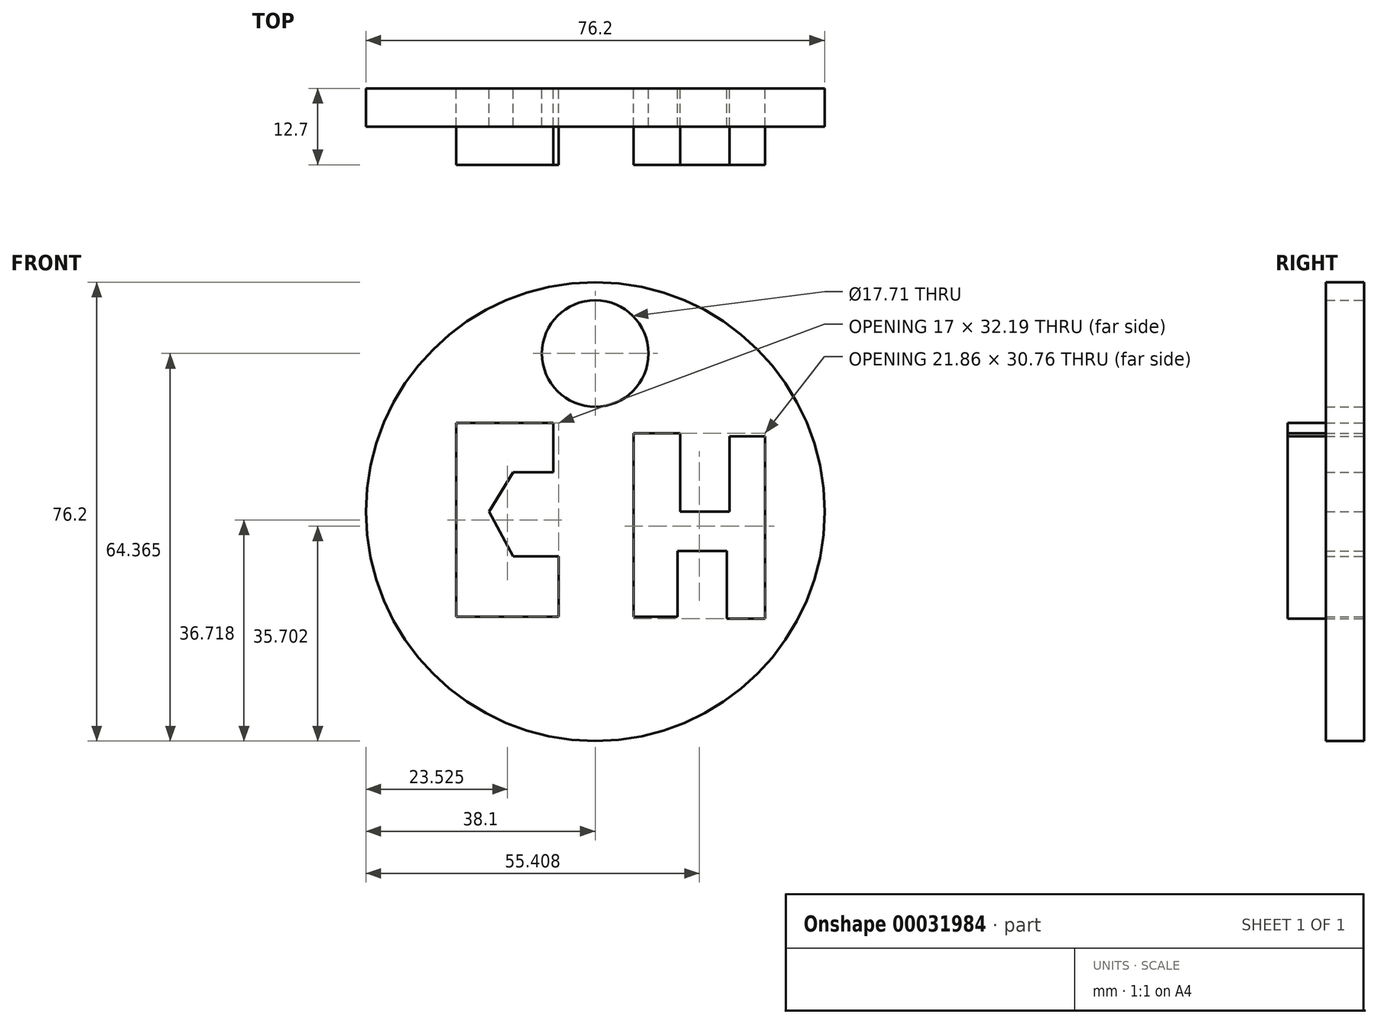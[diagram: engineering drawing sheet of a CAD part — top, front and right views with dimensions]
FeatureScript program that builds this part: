
annotation { "Feature Type Name" : "Feature", "Feature Type Description" : "" }
export const myFeature = defineFeature(function(context is Context, id is Id, definition is map)
    precondition{}
    {
        {
            var Q0;
            Q0=qCreatedBy(makeId("Front.planeOp"),FACE);
            var sketch = newSketch(context, id + "F0", { "sketchPlane" : qUnion([Q0])});
            skCircle(sketch, "E0", {"center": v(0, 0) * mm, "radius": 38.1 * mm});
            skLineSegment(sketch, "E1", {"start": v(6.38, 12.98) * mm, "end": v(14.12, 12.98) * mm});
            skLineSegment(sketch, "E2", {"start": v(14.12, 12.98) * mm, "end": v(14.12, 0) * mm});
            skLineSegment(sketch, "E3", {"start": v(14.12, 0) * mm, "end": v(22.32, 0) * mm});
            skLineSegment(sketch, "E4", {"start": v(22.32, 0) * mm, "end": v(22.32, 12.53) * mm});
            skLineSegment(sketch, "E5", {"start": v(22.32, 12.53) * mm, "end": v(28.24, 12.53) * mm});
            skLineSegment(sketch, "E6", {"start": v(28.24, 12.53) * mm, "end": v(28.24, -17.78) * mm});
            skLineSegment(sketch, "E7", {"start": v(28.24, -17.78) * mm, "end": v(21.86, -17.78) * mm});
            skLineSegment(sketch, "E8", {"start": v(21.86, -17.78) * mm, "end": v(21.86, -6.54) * mm});
            skLineSegment(sketch, "E9", {"start": v(21.86, -6.54) * mm, "end": v(13.66, -6.54) * mm});
            skLineSegment(sketch, "E10", {"start": v(13.66, -6.54) * mm, "end": v(13.66, -17.47) * mm});
            skLineSegment(sketch, "E11", {"start": v(13.66, -17.47) * mm, "end": v(6.38, -17.47) * mm});
            skLineSegment(sketch, "E12", {"start": v(6.38, -17.47) * mm, "end": v(6.38, 12.98) * mm});
            skLineSegment(sketch, "E13", {"start": v(-6.98, 14.71) * mm, "end": v(-23.08, 14.71) * mm});
            skLineSegment(sketch, "E14", {"start": v(-23.08, 14.71) * mm, "end": v(-23.08, -17.48) * mm});
            skLineSegment(sketch, "E15", {"start": v(-23.08, -17.48) * mm, "end": v(-6.07, -17.48) * mm});
            skLineSegment(sketch, "E16", {"start": v(-6.07, -17.48) * mm, "end": v(-6.07, -7.44) * mm});
            skLineSegment(sketch, "E17", {"start": v(-6.07, -7.44) * mm, "end": v(-13.66, -7.44) * mm});
            skLineSegment(sketch, "E18", {"start": v(-13.66, -7.44) * mm, "end": v(-17.61, 0) * mm});
            skLineSegment(sketch, "E19", {"start": v(-17.61, 0) * mm, "end": v(-13.66, 6.53) * mm});
            skLineSegment(sketch, "E20", {"start": v(-13.66, 6.53) * mm, "end": v(-6.98, 6.53) * mm});
            skLineSegment(sketch, "E21", {"start": v(-6.98, 6.53) * mm, "end": v(-6.98, 14.71) * mm});
            skSolve(sketch);
        }
        {
            var Q0;
            Q0=makeQuery(id+"F0.imprint","IMPRINT",FACE,{"disambiguationData":[TD([[makeQuery(id+"F0.imprint","IMPRINT",EDGE,{"derivedFrom":sQuery(id+"F0.wireOp",EDGE,"E13")}),1.0]])]});
            var Q1;
            Q1=makeQuery(id+"F0.imprint","IMPRINT",FACE,{"disambiguationData":[TD([[makeQuery(id+"F0.imprint","IMPRINT",EDGE,{"derivedFrom":sQuery(id+"F0.wireOp",EDGE,"E1")}),-1.0]])]});
            extrude(context, id + "F1", {"entities" : qUnion([Q0, Q1]), "depth" : 12.7 * mm});
        }
        {
            var Q0;
            Q0 = qSketchRegion(id + "F0", true);
            extrude(context, id + "F2", {"entities" : qUnion([Q0]), "depth" : 6.35 * mm});
        }
        {
            var Q0;
            Q0=qCreatedBy(makeId("Front.planeOp"),FACE);
            var sketch = newSketch(context, id + "F3", { "sketchPlane" : qUnion([Q0])});
            skCircle(sketch, "E22", {"center": v(0, 26.27) * mm, "radius": 8.85 * mm});
            skSolve(sketch);
        }
        {
            var Q0;
            Q0=makeQuery(id+"F3.imprint","IMPRINT",FACE,{"disambiguationData":[TD([[makeQuery(id+"F3.imprint","IMPRINT",EDGE,{"derivedFrom":sQuery(id+"F3.wireOp",EDGE,"E22")}),1.0]])]});
            extrude(context, id + "F4", {"entities" : qUnion([Q0]), "operationType" : NewBodyOperationType.REMOVE, "depth" : 25.4 * mm});
        }
    });
